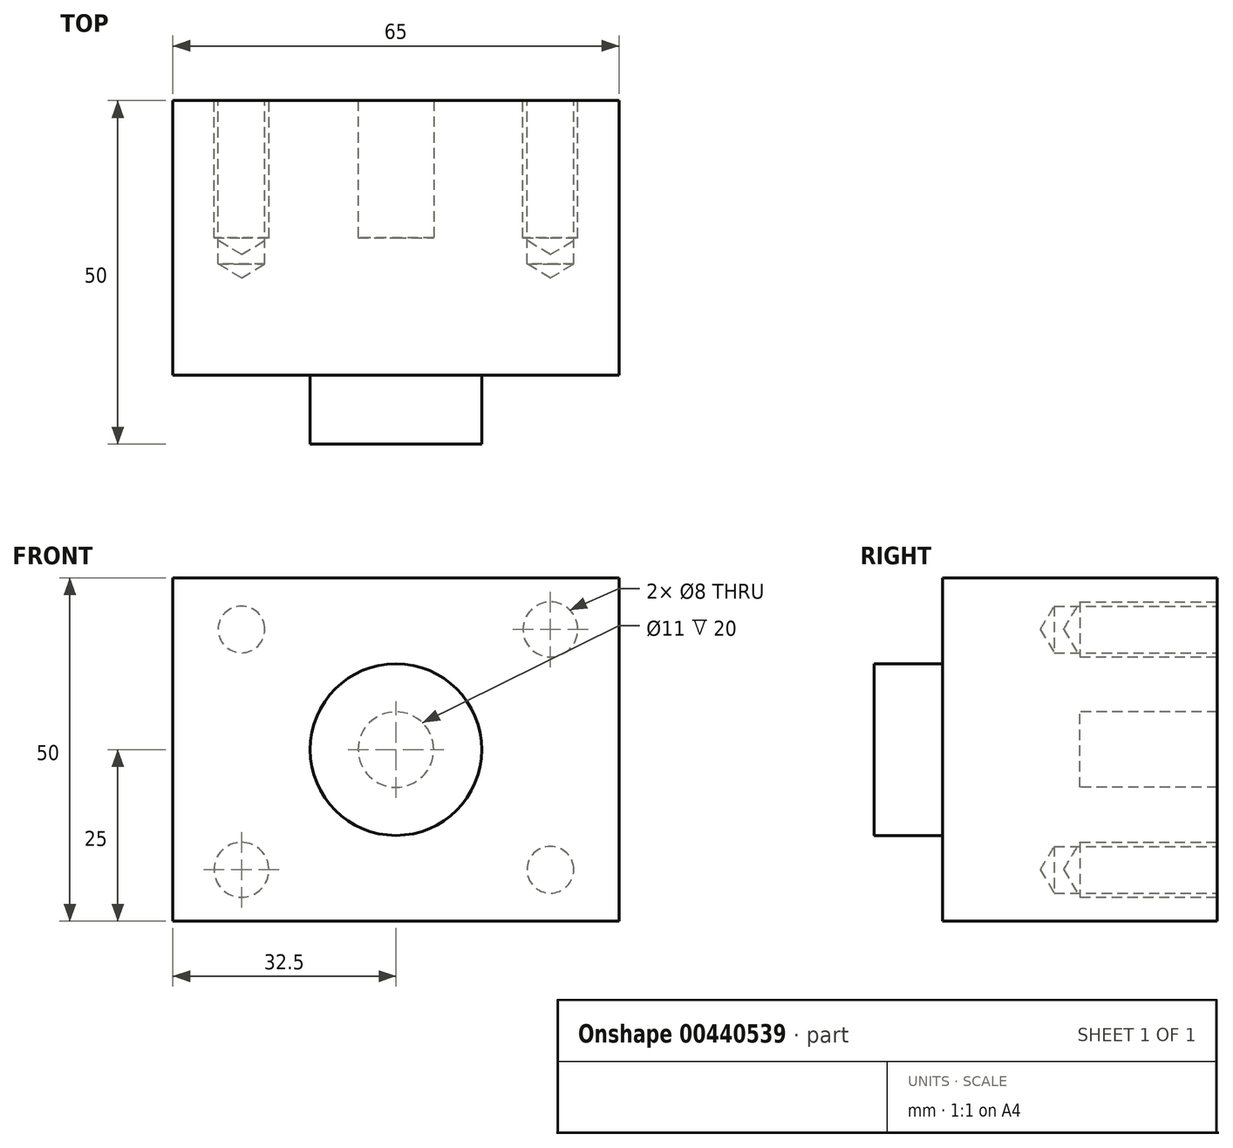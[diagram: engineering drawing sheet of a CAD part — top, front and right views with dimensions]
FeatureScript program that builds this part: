
annotation { "Feature Type Name" : "Feature", "Feature Type Description" : "" }
export const myFeature = defineFeature(function(context is Context, id is Id, definition is map)
    precondition{}
    {
        {
            var Q0;
            Q0=qCreatedBy(makeId("Front.planeOp"),FACE);
            var sketch = newSketch(context, id + "F0", { "sketchPlane" : qUnion([Q0])});
            skLineSegment(sketch, "E0.bottom", {"start": v(32.5, -25) * mm, "end": v(-32.5, -25) * mm});
            skLineSegment(sketch, "E0.top", {"start": v(32.5, 25) * mm, "end": v(-32.5, 25) * mm});
            skLineSegment(sketch, "E0.left", {"start": v(32.5, -25) * mm, "end": v(32.5, 25) * mm});
            skLineSegment(sketch, "E0.right", {"start": v(-32.5, -25) * mm, "end": v(-32.5, 25) * mm});
            skPoint(sketch, "E0.middle", {"position": v(0, 0) * mm});
            skSolve(sketch);
        }
        {
            var Q0;
            Q0=makeQuery(id+"F0.imprint","IMPRINT",FACE,{"disambiguationData":[TD([[makeQuery(id+"F0.imprint","IMPRINT",EDGE,{"derivedFrom":sQuery(id+"F0.wireOp",EDGE,"E0.bottom")}),-1.0]])]});
            extrude(context, id + "F1", {"entities" : qUnion([Q0]), "endBound" : BoundingType.SYMMETRIC, "oppositeDirection" : true, "depth" : 40 * mm});
        }
        {
            var Q0;
            Q0=makeQuery(id+"F1.opExtrude","CAP_FACE",FACE,{"disambiguationData":[OSD([sQuery(id+"F0.wireOp",EDGE,"E0.bottom"),sQuery(id+"F0.wireOp",EDGE,"E0.top"),sQuery(id+"F0.wireOp",EDGE,"E0.left"),sQuery(id+"F0.wireOp",EDGE,"E0.right")])],"isStart":true});
            var sketch = newSketch(context, id + "F2", { "sketchPlane" : qUnion([Q0])});
            skCircle(sketch, "E1", {"center": v(0, 0) * mm, "radius": 12.5 * mm});
            skSolve(sketch);
        }
        {
            var Q0;
            Q0 = qSketchRegion(id + "F2", true);
            extrude(context, id + "F3", {"entities" : qUnion([Q0]), "operationType" : NewBodyOperationType.ADD, "depth" : 10 * mm});
        }
        {
            var Q0;
            Q0=sQuery(id+"F0.wireOp",VERTEX,"E0.middle");
            var Q1;
            Q1=makeQuery(id+"F1.opExtrude","SWEPT_BODY",BODY,{"disambiguationData":[OSD([sQuery(id+"F0.wireOp",EDGE,"E0.bottom"),sQuery(id+"F0.wireOp",EDGE,"E0.top"),sQuery(id+"F0.wireOp",EDGE,"E0.left"),sQuery(id+"F0.wireOp",EDGE,"E0.right")])]});
            hole(context, id + "F4", {"style" : HoleStyle.SIMPLE, "endStyle" : HoleEndStyle.BLIND, "holeDiameter" : 11 * mm, "holeDepth" : 60 * mm, "isTappedThrough" : true, "tappedDepth" : 12 * mm, "tapClearance" : 3, "locations" : qUnion([Q0]), "scope" : qUnion([Q1])});
        }
        {
            var Q0;
            Q0=makeQuery(id+"F1.opExtrude","CAP_FACE",FACE,{"disambiguationData":[OSD([sQuery(id+"F0.wireOp",EDGE,"E0.bottom"),sQuery(id+"F0.wireOp",EDGE,"E0.top"),sQuery(id+"F0.wireOp",EDGE,"E0.left"),sQuery(id+"F0.wireOp",EDGE,"E0.right")])],"isStart":false});
            var sketch = newSketch(context, id + "F5", { "sketchPlane" : qUnion([Q0])});
            skPoint(sketch, "E2", {"position": v(-22.5, 17.5) * mm});
            skPoint(sketch, "E3", {"position": v(22.5, 17.5) * mm});
            skPoint(sketch, "E4", {"position": v(22.5, -17.5) * mm});
            skPoint(sketch, "E5", {"position": v(-22.5, -17.5) * mm});
            skLineSegment(sketch, "E6", {"start": v(0, -25) * mm, "end": v(0, 25) * mm, "construction": true});
            skLineSegment(sketch, "E7", {"start": v(0, 0) * mm, "end": v(32.5, 0) * mm, "construction": true});
            skSolve(sketch);
        }
        {
            var Q0;
            Q0=sQuery(id+"F5.wireOp",VERTEX,"E5");
            var Q1;
            Q1=sQuery(id+"F5.wireOp",VERTEX,"E3");
            var Q2;
            Q2=makeQuery(id+"F1.opExtrude","SWEPT_BODY",BODY,{"disambiguationData":[OSD([sQuery(id+"F0.wireOp",EDGE,"E0.bottom"),sQuery(id+"F0.wireOp",EDGE,"E0.top"),sQuery(id+"F0.wireOp",EDGE,"E0.left"),sQuery(id+"F0.wireOp",EDGE,"E0.right")])]});
            hole(context, id + "F6", {"style" : HoleStyle.SIMPLE, "endStyle" : HoleEndStyle.BLIND, "standardTappedOrClearance" : lookupTablePath({ "standard" : "ISO", "engagement" : "75%", "pitch" : "1.25 mm", "size" : "M8", "type" : "Tapped" }), "standardBlindInLast" : lookupTablePath({ "standard" : "ISO", "engagement" : "75%", "pitch" : "1.25 mm", "size" : "M8", "type" : "Tapped" }), "holeDiameter" : 6.8 * mm, "showTappedDepth" : true, "holeDepth" : 23.75 * mm, "tappedDepth" : 20 * mm, "tapClearance" : 3, "locations" : qUnion([Q0, Q1]), "scope" : qUnion([Q2]), "majorDiameter" : 8 * mm});
        }
        {
            var Q0;
            Q0=sQuery(id+"F5.wireOp",VERTEX,"E2");
            var Q1;
            Q1=sQuery(id+"F5.wireOp",VERTEX,"E4");
            var Q2;
            Q2=makeQuery(id+"F1.opExtrude","SWEPT_BODY",BODY,{"disambiguationData":[OSD([sQuery(id+"F0.wireOp",EDGE,"E0.bottom"),sQuery(id+"F0.wireOp",EDGE,"E0.top"),sQuery(id+"F0.wireOp",EDGE,"E0.left"),sQuery(id+"F0.wireOp",EDGE,"E0.right")])]});
            hole(context, id + "F7", {"style" : HoleStyle.SIMPLE, "endStyle" : HoleEndStyle.BLIND, "standardTappedOrClearance" : lookupTablePath({ "standard" : "ISO", "size" : "8", "type" : "Drilled" }), "standardBlindInLast" : lookupTablePath({ "standard" : "ISO", "size" : "8", "type" : "Drilled" }), "holeDiameter" : 8 * mm, "holeDepth" : 20 * mm, "isTappedThrough" : true, "tappedDepth" : 12 * mm, "tapClearance" : 3, "locations" : qUnion([Q0, Q1]), "scope" : qUnion([Q2])});
        }
    });
